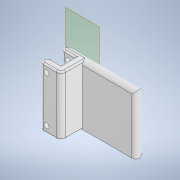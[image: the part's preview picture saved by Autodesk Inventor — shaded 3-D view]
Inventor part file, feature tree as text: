
AUTODESK INVENTOR PART (.ipt)
format: ipt  version: 2020.3 (Build 243373000, 373)  size: 199,680 bytes
history: native  units: mm
features: fillet x4, sketch x4, extrude x3, other x2, hole x1
ambient origin geometry x8: Origin, YZ Plane, XZ Plane, XY Plane, X Axis, Y Axis, Z Axis, Center Point
bodies: Body1 (feature_tree)
feature tree (14):
  other  "ソリッド1"
  extrude  "押し出し1"  Depth=5.0mm TaperAngle=0.0deg
  extrude  "押し出し2"  Depth=39.0mm
  extrude  "押し出し3"  Depth=49.0mm
  fillet  "フィレット2"  Radius=5.0mm
  other  "作業平面1"
  hole  "穴1"  [1 undecoded]
  fillet  "フィレット5"  Radius=9.0mm
  fillet  "フィレット6"  Radius=9.0mm
  fillet  "フィレット7"  Radius=5.0mm
  sketch  "スケッチ1"
  sketch  "スケッチ2"
  sketch  "スケッチ3"
  sketch  "スケッチ6"
note: 1 required parameter value undecoded (feature->parameter linkage not recoverable at this tier; creation-order binding heuristic only, values carry confidence <= 0.55)
